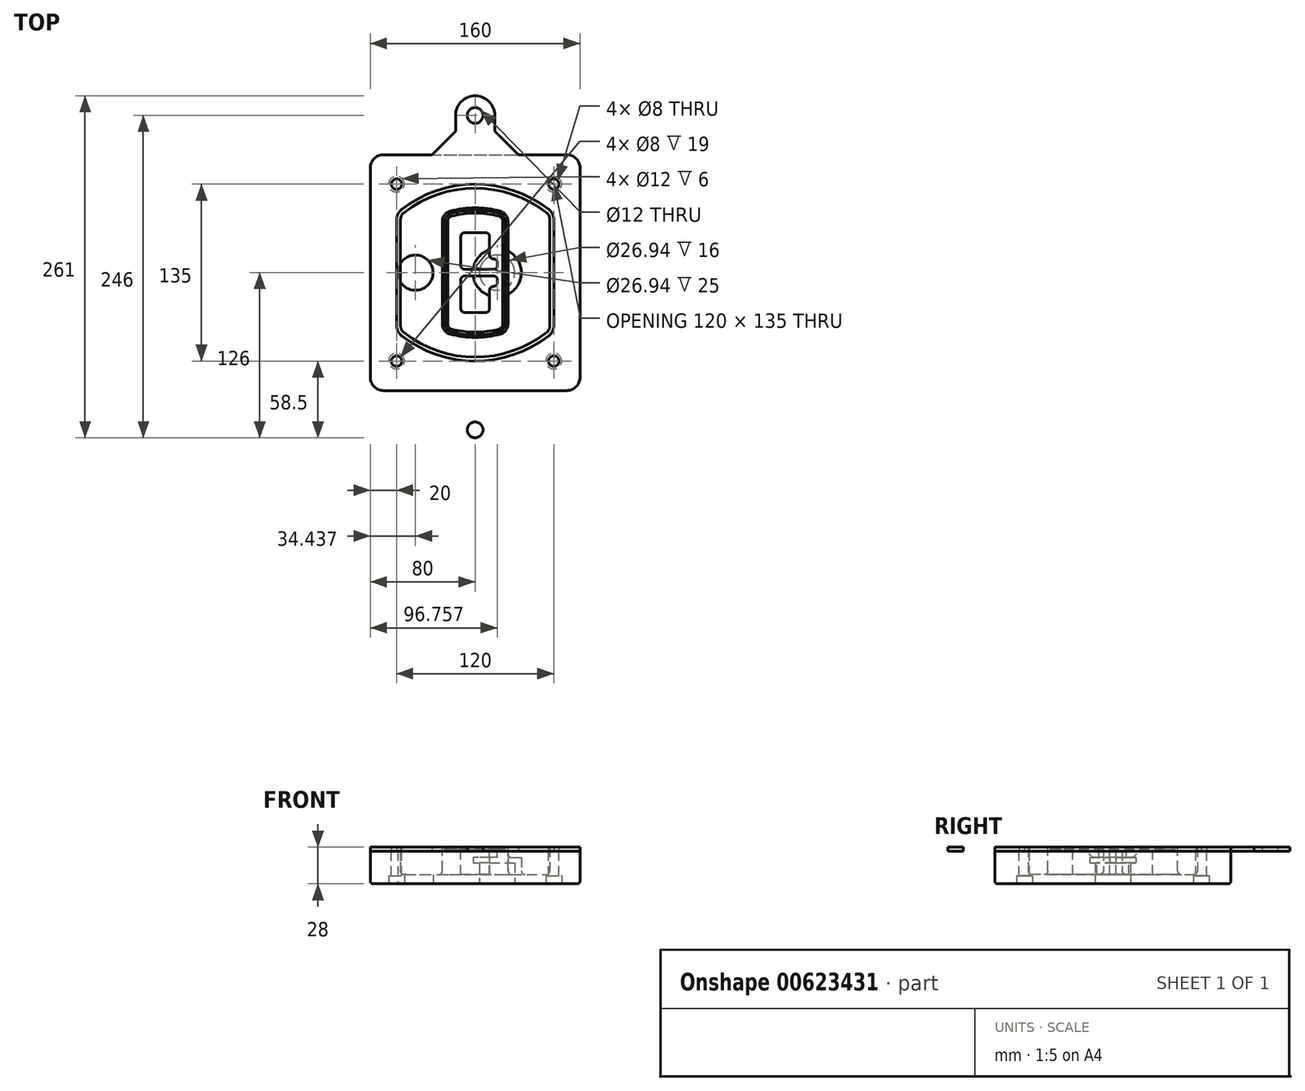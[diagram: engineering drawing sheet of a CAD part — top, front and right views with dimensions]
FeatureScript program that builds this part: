
annotation { "Feature Type Name" : "Feature", "Feature Type Description" : "" }
export const myFeature = defineFeature(function(context is Context, id is Id, definition is map)
    precondition{}
    {
        {
            var Q0;
            Q0=qCreatedBy(makeId("Top.planeOp"),FACE);
            var sketch = newSketch(context, id + "F0", { "sketchPlane" : qUnion([Q0])});
            skPoint(sketch, "E0.rect.middle", {"position": v(0, 0) * mm});
            skLineSegment(sketch, "E1.bottom", {"start": v(-70, -90) * mm, "end": v(70, -90) * mm});
            skLineSegment(sketch, "E1.top", {"start": v(-70, 90) * mm, "end": v(70, 90) * mm});
            skLineSegment(sketch, "E1.left", {"start": v(-80, -80) * mm, "end": v(-80, 80) * mm});
            skLineSegment(sketch, "E1.right", {"start": v(80, -80) * mm, "end": v(80, 80) * mm});
            skLineSegment(sketch, "E2", {"start": v(-80, 90) * mm, "end": v(80, -90) * mm, "construction": true});
            skLineSegment(sketch, "E3", {"start": v(80, 90) * mm, "end": v(-80, -90) * mm, "construction": true});
            skCircle(sketch, "E4", {"center": v(-60, 67.5) * mm, "radius": 4 * mm});
            skCircle(sketch, "E5", {"center": v(60, 67.5) * mm, "radius": 4 * mm});
            skCircle(sketch, "E6", {"center": v(60, -67.5) * mm, "radius": 4 * mm});
            skCircle(sketch, "E7", {"center": v(-60, -67.5) * mm, "radius": 4 * mm});
            skLineSegment(sketch, "E8", {"start": v(-60, 67.5) * mm, "end": v(60, 67.5) * mm, "construction": true});
            skLineSegment(sketch, "E9", {"start": v(60, 67.5) * mm, "end": v(60, -67.5) * mm, "construction": true});
            skLineSegment(sketch, "E10", {"start": v(60, -67.5) * mm, "end": v(-60, -67.5) * mm, "construction": true});
            skLineSegment(sketch, "E11", {"start": v(-60, -67.5) * mm, "end": v(-60, 67.5) * mm, "construction": true});
            skLineSegment(sketch, "E12", {"start": v(-60, 40.3) * mm, "end": v(-60, -40.3) * mm});
            skLineSegment(sketch, "E13", {"start": v(60, 40.3) * mm, "end": v(60, -40.3) * mm});
            skArc(sketch, "E14", {"start": v(56.15, 48.18) * mm, "mid": v(0, 67.5) * mm, "end": v(-56.15, 48.18) * mm});
            skArc(sketch, "E15", {"start": v(-56.15, -48.18) * mm, "mid": v(0, -67.5) * mm, "end": v(56.15, -48.18) * mm});
            skLineSegment(sketch, "E16", {"start": v(-60, 0) * mm, "end": v(60, 0) * mm, "construction": true});
            skPoint(sketch, "E17.visualSharp", {"position": v(-60, -45) * mm});
            skArc(sketch, "E17.filletArc", {"start": v(-60, -40.3) * mm, "mid": v(-58.99, -44.68) * mm, "end": v(-56.15, -48.18) * mm});
            skPoint(sketch, "E18.visualSharp", {"position": v(-60, 45) * mm});
            skArc(sketch, "E18.filletArc", {"start": v(-56.15, 48.18) * mm, "mid": v(-58.99, 44.68) * mm, "end": v(-60, 40.3) * mm});
            skPoint(sketch, "E19.visualSharp", {"position": v(60, 45) * mm});
            skArc(sketch, "E19.filletArc", {"start": v(60, 40.3) * mm, "mid": v(58.99, 44.68) * mm, "end": v(56.15, 48.18) * mm});
            skPoint(sketch, "E20.visualSharp", {"position": v(60, -45) * mm});
            skArc(sketch, "E20.filletArc", {"start": v(56.15, -48.18) * mm, "mid": v(58.99, -44.68) * mm, "end": v(60, -40.3) * mm});
            skPoint(sketch, "E21.visualSharp", {"position": v(-80, 90) * mm});
            skArc(sketch, "E21.filletArc", {"start": v(-70, 90) * mm, "mid": v(-77.07, 87.07) * mm, "end": v(-80, 80) * mm});
            skPoint(sketch, "E22.visualSharp", {"position": v(80, 90) * mm});
            skArc(sketch, "E22.filletArc", {"start": v(80, 80) * mm, "mid": v(77.07, 87.07) * mm, "end": v(70, 90) * mm});
            skPoint(sketch, "E23.visualSharp", {"position": v(80, -90) * mm});
            skArc(sketch, "E23.filletArc", {"start": v(70, -90) * mm, "mid": v(77.07, -87.07) * mm, "end": v(80, -80) * mm});
            skPoint(sketch, "E24.visualSharp", {"position": v(-80, -90) * mm});
            skArc(sketch, "E24.filletArc", {"start": v(-80, -80) * mm, "mid": v(-77.07, -87.07) * mm, "end": v(-70, -90) * mm});
            skArc(sketch, "E25.0", {"start": v(57, 40.3) * mm, "mid": v(56.3, 43.36) * mm, "end": v(54.3, 45.81) * mm});
            skLineSegment(sketch, "E25.1", {"start": v(57, 40.3) * mm, "end": v(57, -40.3) * mm});
            skArc(sketch, "E25.2", {"start": v(54.3, -45.81) * mm, "mid": v(56.3, -43.36) * mm, "end": v(57, -40.3) * mm});
            skArc(sketch, "E25.3", {"start": v(-54.3, -45.81) * mm, "mid": v(0, -64.5) * mm, "end": v(54.3, -45.81) * mm});
            skArc(sketch, "E25.4", {"start": v(-57, -40.3) * mm, "mid": v(-56.3, -43.36) * mm, "end": v(-54.3, -45.81) * mm});
            skArc(sketch, "E25.5", {"start": v(54.3, 45.81) * mm, "mid": v(0, 64.5) * mm, "end": v(-54.3, 45.81) * mm});
            skLineSegment(sketch, "E25.6", {"start": v(-57, 40.3) * mm, "end": v(-57, -40.3) * mm});
            skArc(sketch, "E25.7", {"start": v(-54.3, 45.81) * mm, "mid": v(-56.3, 43.36) * mm, "end": v(-57, 40.3) * mm});
            skArc(sketch, "E26.0", {"start": v(-58.62, 51.33) * mm, "mid": v(-62.58, 46.43) * mm, "end": v(-64, 40.3) * mm});
            skArc(sketch, "E26.1", {"start": v(58.62, 51.33) * mm, "mid": v(0, 71.5) * mm, "end": v(-58.62, 51.33) * mm});
            skArc(sketch, "E26.2", {"start": v(64, 40.3) * mm, "mid": v(62.58, 46.43) * mm, "end": v(58.62, 51.33) * mm});
            skLineSegment(sketch, "E26.3", {"start": v(64, 40.3) * mm, "end": v(64, -40.3) * mm});
            skArc(sketch, "E26.4", {"start": v(58.62, -51.33) * mm, "mid": v(62.58, -46.43) * mm, "end": v(64, -40.3) * mm});
            skLineSegment(sketch, "E26.5", {"start": v(-64, 40.3) * mm, "end": v(-64, -40.3) * mm});
            skArc(sketch, "E26.6", {"start": v(-58.62, -51.33) * mm, "mid": v(0, -71.5) * mm, "end": v(58.62, -51.33) * mm});
            skArc(sketch, "E26.7", {"start": v(-64, -40.3) * mm, "mid": v(-62.58, -46.43) * mm, "end": v(-58.62, -51.33) * mm});
            skSolve(sketch);
        }
        {
            var Q0;
            Q0=makeQuery(id+"F0.imprint","IMPRINT",FACE,{"disambiguationData":[TD([[makeQuery(id+"F0.imprint","IMPRINT",EDGE,{"derivedFrom":sQuery(id+"F0.wireOp",EDGE,"E1.bottom")}),1.0]])]});
            var Q1;
            Q1=makeQuery(id+"F0.imprint","IMPRINT",FACE,{"disambiguationData":[TD([[makeQuery(id+"F0.imprint","IMPRINT",EDGE,{"derivedFrom":sQuery(id+"F0.wireOp",EDGE,"E12")}),1.0]])]});
            var Q2;
            Q2=makeQuery(id+"F0.imprint","IMPRINT",FACE,{"disambiguationData":[TD([[makeQuery(id+"F0.imprint","IMPRINT",EDGE,{"derivedFrom":sQuery(id+"F0.wireOp",EDGE,"E25.0")}),1.0]])]});
            var Q3;
            Q3=makeQuery(id+"F0.imprint","IMPRINT",FACE,{"disambiguationData":[TD([[makeQuery(id+"F0.imprint","IMPRINT",EDGE,{"derivedFrom":sQuery(id+"F0.wireOp",EDGE,"E12")}),-1.0]])]});
            extrude(context, id + "F1", {"entities" : qUnion([Q0, Q1, Q2, Q3]), "oppositeDirection" : true, "depth" : 25 * mm});
        }
        {
            var Q0;
            Q0=makeQuery(id+"F0.imprint","IMPRINT",FACE,{"disambiguationData":[TD([[makeQuery(id+"F0.imprint","IMPRINT",EDGE,{"derivedFrom":sQuery(id+"F0.wireOp",EDGE,"E12")}),1.0]])]});
            extrude(context, id + "F2", {"entities" : qUnion([Q0]), "operationType" : NewBodyOperationType.ADD, "depth" : 3 * mm});
        }
        {
            var Q0;
            Q0=makeQuery(id+"F0.imprint","IMPRINT",FACE,{"disambiguationData":[TD([[makeQuery(id+"F0.imprint","IMPRINT",EDGE,{"derivedFrom":sQuery(id+"F0.wireOp",EDGE,"E25.0")}),1.0]])]});
            extrude(context, id + "F3", {"entities" : qUnion([Q0]), "operationType" : NewBodyOperationType.REMOVE, "oppositeDirection" : true, "depth" : 18 * mm});
        }
        {
            var Q0;
            Q0=makeQuery(id+"F2.opExtrude","CAP_FACE",FACE,{"disambiguationData":[OSD([sQuery(id+"F0.wireOp",EDGE,"E12"),sQuery(id+"F0.wireOp",EDGE,"E13"),sQuery(id+"F0.wireOp",EDGE,"E14"),sQuery(id+"F0.wireOp",EDGE,"E15"),sQuery(id+"F0.wireOp",EDGE,"E17.filletArc"),sQuery(id+"F0.wireOp",EDGE,"E18.filletArc"),sQuery(id+"F0.wireOp",EDGE,"E19.filletArc"),sQuery(id+"F0.wireOp",EDGE,"E20.filletArc"),sQuery(id+"F0.wireOp",EDGE,"E25.0"),sQuery(id+"F0.wireOp",EDGE,"E25.1"),sQuery(id+"F0.wireOp",EDGE,"E25.2"),sQuery(id+"F0.wireOp",EDGE,"E25.3"),sQuery(id+"F0.wireOp",EDGE,"E25.4"),sQuery(id+"F0.wireOp",EDGE,"E25.5"),sQuery(id+"F0.wireOp",EDGE,"E25.6"),sQuery(id+"F0.wireOp",EDGE,"E25.7")])],"isStart":false});
            var sketch = newSketch(context, id + "F4", { "sketchPlane" : qUnion([Q0])});
            skArc(sketch, "E27.0", {"start": v(-19.08, -46.97) * mm, "mid": v(0, -49.5) * mm, "end": v(19.08, -46.97) * mm});
            skArc(sketch, "E28.0", {"start": v(19.08, 46.97) * mm, "mid": v(0, 49.5) * mm, "end": v(-19.08, 46.97) * mm});
            skLineSegment(sketch, "E29", {"start": v(-25, 39.25) * mm, "end": v(-25, -39.25) * mm});
            skLineSegment(sketch, "E30", {"start": v(25, 39.25) * mm, "end": v(25, -39.25) * mm});
            skLineSegment(sketch, "E31", {"start": v(-25, 45.1) * mm, "end": v(25, 45.1) * mm, "construction": true});
            skLineSegment(sketch, "E32", {"start": v(-25, -45.1) * mm, "end": v(25, -45.1) * mm, "construction": true});
            skPoint(sketch, "E33.visualSharp", {"position": v(-25, 45.1) * mm});
            skArc(sketch, "E33.filletArc", {"start": v(-19.08, 46.97) * mm, "mid": v(-23.35, 44.11) * mm, "end": v(-25, 39.25) * mm});
            skPoint(sketch, "E34.visualSharp", {"position": v(25, 45.1) * mm});
            skArc(sketch, "E34.filletArc", {"start": v(25, 39.25) * mm, "mid": v(23.35, 44.11) * mm, "end": v(19.08, 46.97) * mm});
            skPoint(sketch, "E35.visualSharp", {"position": v(25, -45.1) * mm});
            skArc(sketch, "E35.filletArc", {"start": v(19.08, -46.97) * mm, "mid": v(23.35, -44.11) * mm, "end": v(25, -39.25) * mm});
            skPoint(sketch, "E36.visualSharp", {"position": v(-25, -45.1) * mm});
            skArc(sketch, "E36.filletArc", {"start": v(-25, -39.25) * mm, "mid": v(-23.35, -44.11) * mm, "end": v(-19.08, -46.97) * mm});
            skArc(sketch, "E37.0", {"start": v(54.3, 45.81) * mm, "mid": v(0, 64.5) * mm, "end": v(-54.3, 45.81) * mm});
            skArc(sketch, "E37.1", {"start": v(-54.3, 45.81) * mm, "mid": v(-56.3, 43.36) * mm, "end": v(-57, 40.3) * mm});
            skLineSegment(sketch, "E37.2", {"start": v(-57, 40.3) * mm, "end": v(-57, -40.3) * mm});
            skArc(sketch, "E37.3", {"start": v(-57, -40.3) * mm, "mid": v(-56.3, -43.36) * mm, "end": v(-54.3, -45.81) * mm});
            skArc(sketch, "E37.4", {"start": v(-54.3, -45.81) * mm, "mid": v(0, -64.5) * mm, "end": v(54.3, -45.81) * mm});
            skArc(sketch, "E37.5", {"start": v(54.3, -45.81) * mm, "mid": v(56.3, -43.36) * mm, "end": v(57, -40.3) * mm});
            skLineSegment(sketch, "E37.6", {"start": v(57, 40.3) * mm, "end": v(57, -40.3) * mm});
            skArc(sketch, "E37.7", {"start": v(57, 40.3) * mm, "mid": v(56.3, 43.36) * mm, "end": v(54.3, 45.81) * mm});
            skLineSegment(sketch, "E38.0", {"start": v(23, 39.25) * mm, "end": v(23, -39.25) * mm});
            skArc(sketch, "E38.1", {"start": v(18.56, -45.04) * mm, "mid": v(21.76, -42.9) * mm, "end": v(23, -39.25) * mm});
            skArc(sketch, "E38.2", {"start": v(-18.56, -45.04) * mm, "mid": v(0, -47.5) * mm, "end": v(18.56, -45.04) * mm});
            skArc(sketch, "E38.3", {"start": v(-23, -39.25) * mm, "mid": v(-21.76, -42.9) * mm, "end": v(-18.56, -45.04) * mm});
            skLineSegment(sketch, "E38.4", {"start": v(-23, 39.25) * mm, "end": v(-23, -39.25) * mm});
            skArc(sketch, "E38.5", {"start": v(23, 39.25) * mm, "mid": v(21.76, 42.9) * mm, "end": v(18.56, 45.04) * mm});
            skArc(sketch, "E38.6", {"start": v(-18.56, 45.04) * mm, "mid": v(-21.76, 42.9) * mm, "end": v(-23, 39.25) * mm});
            skArc(sketch, "E38.7", {"start": v(18.56, 45.04) * mm, "mid": v(0, 47.5) * mm, "end": v(-18.56, 45.04) * mm});
            skArc(sketch, "E39.0", {"start": v(21, 39.25) * mm, "mid": v(20.18, 41.68) * mm, "end": v(18.04, 43.1) * mm});
            skLineSegment(sketch, "E39.1", {"start": v(21, 39.25) * mm, "end": v(21, -39.25) * mm});
            skArc(sketch, "E39.2", {"start": v(18.04, -43.1) * mm, "mid": v(20.18, -41.68) * mm, "end": v(21, -39.25) * mm});
            skArc(sketch, "E39.3", {"start": v(-18.04, -43.1) * mm, "mid": v(0, -45.5) * mm, "end": v(18.04, -43.1) * mm});
            skArc(sketch, "E39.4", {"start": v(-21, -39.25) * mm, "mid": v(-20.18, -41.68) * mm, "end": v(-18.04, -43.1) * mm});
            skArc(sketch, "E39.5", {"start": v(18.04, 43.1) * mm, "mid": v(0, 45.5) * mm, "end": v(-18.04, 43.1) * mm});
            skLineSegment(sketch, "E39.6", {"start": v(-21, 39.25) * mm, "end": v(-21, -39.25) * mm});
            skArc(sketch, "E39.7", {"start": v(-18.04, 43.1) * mm, "mid": v(-20.18, 41.68) * mm, "end": v(-21, 39.25) * mm});
            skLineSegment(sketch, "E40", {"start": v(-25, 0) * mm, "end": v(25, 0) * mm, "construction": true});
            skLineSegment(sketch, "E41", {"start": v(-11, 5.5) * mm, "end": v(-11, 27.5) * mm});
            skLineSegment(sketch, "E42", {"start": v(-8, 30.5) * mm, "end": v(8, 30.5) * mm});
            skLineSegment(sketch, "E43", {"start": v(11, 27.5) * mm, "end": v(11, 13.5) * mm});
            skLineSegment(sketch, "E44", {"start": v(14, 10.5) * mm, "end": v(14, 10.5) * mm});
            skLineSegment(sketch, "E45", {"start": v(17, 7.5) * mm, "end": v(17, 5.5) * mm});
            skLineSegment(sketch, "E46", {"start": v(14, 2.5) * mm, "end": v(-8, 2.5) * mm});
            skPoint(sketch, "E47.visualSharp", {"position": v(-11, 30.5) * mm});
            skArc(sketch, "E47.filletArc", {"start": v(-8, 30.5) * mm, "mid": v(-10.12, 29.62) * mm, "end": v(-11, 27.5) * mm});
            skPoint(sketch, "E48.visualSharp", {"position": v(11, 30.5) * mm});
            skArc(sketch, "E48.filletArc", {"start": v(11, 27.5) * mm, "mid": v(10.12, 29.62) * mm, "end": v(8, 30.5) * mm});
            skPoint(sketch, "E49.visualSharp", {"position": v(11, 10.5) * mm});
            skArc(sketch, "E49.filletArc", {"start": v(11, 13.5) * mm, "mid": v(11.88, 11.38) * mm, "end": v(14, 10.5) * mm});
            skPoint(sketch, "E50.visualSharp", {"position": v(17, 10.5) * mm});
            skArc(sketch, "E50.filletArc", {"start": v(17, 7.5) * mm, "mid": v(16.12, 9.62) * mm, "end": v(14, 10.5) * mm});
            skPoint(sketch, "E51.visualSharp", {"position": v(17, 2.5) * mm});
            skArc(sketch, "E51.filletArc", {"start": v(14, 2.5) * mm, "mid": v(16.12, 3.38) * mm, "end": v(17, 5.5) * mm});
            skPoint(sketch, "E52.visualSharp", {"position": v(-11, 2.5) * mm});
            skArc(sketch, "E52.filletArc", {"start": v(-11, 5.5) * mm, "mid": v(-10.12, 3.38) * mm, "end": v(-8, 2.5) * mm});
            skLineSegment(sketch, "E53.0.MirrorCS", {"start": v(14, -2.5) * mm, "end": v(-8, -2.5) * mm});
            skArc(sketch, "E54.0.MirrorCS", {"start": v(-11, -5.5) * mm, "mid": v(-10.12, -3.38) * mm, "end": v(-8, -2.5) * mm});
            skLineSegment(sketch, "E55.0.MirrorCS", {"start": v(-11, -5.5) * mm, "end": v(-11, -27.5) * mm});
            skArc(sketch, "E56.0.MirrorCS", {"start": v(-8, -30.5) * mm, "mid": v(-10.12, -29.62) * mm, "end": v(-11, -27.5) * mm});
            skLineSegment(sketch, "E57.0.MirrorCS", {"start": v(-8, -30.5) * mm, "end": v(8, -30.5) * mm});
            skArc(sketch, "E58.0.MirrorCS", {"start": v(11, -27.5) * mm, "mid": v(10.12, -29.62) * mm, "end": v(8, -30.5) * mm});
            skLineSegment(sketch, "E59.0.MirrorCS", {"start": v(11, -27.5) * mm, "end": v(11, -13.5) * mm});
            skArc(sketch, "E60.0.MirrorCS", {"start": v(11, -13.5) * mm, "mid": v(11.88, -11.38) * mm, "end": v(14, -10.5) * mm});
            skArc(sketch, "E61.0.MirrorCS", {"start": v(17, -7.5) * mm, "mid": v(16.12, -9.62) * mm, "end": v(14, -10.5) * mm});
            skLineSegment(sketch, "E62.0.MirrorCS", {"start": v(17, -7.5) * mm, "end": v(17, -5.5) * mm});
            skArc(sketch, "E63.0.MirrorCS", {"start": v(14, -2.5) * mm, "mid": v(16.12, -3.38) * mm, "end": v(17, -5.5) * mm});
            skSolve(sketch);
        }
        {
            var Q0;
            Q0=makeQuery(id+"F4.imprint","IMPRINT",FACE,{"disambiguationData":[TD([[makeQuery(id+"F4.imprint","IMPRINT",EDGE,{"derivedFrom":sQuery(id+"F4.wireOp",EDGE,"E27.0")}),1.0]])]});
            var Q1;
            Q1=makeQuery(id+"F4.imprint","IMPRINT",FACE,{"disambiguationData":[TD([[makeQuery(id+"F4.imprint","IMPRINT",EDGE,{"derivedFrom":sQuery(id+"F4.wireOp",EDGE,"E38.0")}),-1.0]])]});
            var Q2;
            Q2=makeQuery(id+"F4.imprint","IMPRINT",FACE,{"disambiguationData":[TD([[makeQuery(id+"F4.imprint","IMPRINT",EDGE,{"derivedFrom":sQuery(id+"F4.wireOp",EDGE,"E39.0")}),1.0]])]});
            extrude(context, id + "F5", {"entities" : qUnion([Q0, Q1, Q2]), "operationType" : NewBodyOperationType.ADD, "endBound" : BoundingType.UP_TO_NEXT, "oppositeDirection" : true, "depth" : 25 * mm});
        }
        {
            var Q0;
            Q0=makeQuery(id+"F4.imprint","IMPRINT",FACE,{"disambiguationData":[TD([[makeQuery(id+"F4.imprint","IMPRINT",EDGE,{"derivedFrom":sQuery(id+"F4.wireOp",EDGE,"E38.0")}),-1.0]])]});
            extrude(context, id + "F6", {"entities" : qUnion([Q0]), "operationType" : NewBodyOperationType.REMOVE, "oppositeDirection" : true, "depth" : 2 * mm});
        }
        {
            var Q0;
            Q0=makeQuery(id+"F1.opExtrude","CAP_FACE",FACE,{"disambiguationData":[OSD([sQuery(id+"F0.wireOp",EDGE,"E1.bottom"),sQuery(id+"F0.wireOp",EDGE,"E1.top"),sQuery(id+"F0.wireOp",EDGE,"E1.left"),sQuery(id+"F0.wireOp",EDGE,"E1.right"),sQuery(id+"F0.wireOp",EDGE,"E4"),sQuery(id+"F0.wireOp",EDGE,"E5"),sQuery(id+"F0.wireOp",EDGE,"E6"),sQuery(id+"F0.wireOp",EDGE,"E7"),sQuery(id+"F0.wireOp",EDGE,"E21.filletArc"),sQuery(id+"F0.wireOp",EDGE,"E22.filletArc"),sQuery(id+"F0.wireOp",EDGE,"E23.filletArc"),sQuery(id+"F0.wireOp",EDGE,"E24.filletArc")])],"isStart":false});
            var sketch = newSketch(context, id + "F7", { "sketchPlane" : qUnion([Q0])});
            skCircle(sketch, "E64", {"center": v(16.76, 0) * mm, "radius": 13.47 * mm});
            skCircle(sketch, "E65", {"center": v(-45.56, 0) * mm, "radius": 13.47 * mm});
            skLineSegment(sketch, "E66", {"start": v(80, 0) * mm, "end": v(-80, 0) * mm});
            skCircle(sketch, "E67", {"center": v(16.76, 0) * mm, "radius": 18.47 * mm});
            skCircle(sketch, "E68", {"center": v(60, -67.5) * mm, "radius": 6 * mm});
            skCircle(sketch, "E69", {"center": v(-60, -67.5) * mm, "radius": 6 * mm});
            skCircle(sketch, "E70", {"center": v(-60, 67.5) * mm, "radius": 6 * mm});
            skCircle(sketch, "E71", {"center": v(60, 67.5) * mm, "radius": 6 * mm});
            skSolve(sketch);
        }
        {
            var Q0;
            {var subQ1=sQuery(id+"F7.wireOp",EDGE,"E66");var subQ4=sQuery(id+"F7.wireOp",EDGE,"E64");var subQ6=makeQuery(id+"F7.imprint","INTERSECT",VERTEX,{"disambiguationData":[OD(0.0)],"derivedFrom":[subQ4,subQ1]});Q0=makeQuery(id+"F7.imprint","IMPRINT",FACE,{"disambiguationData":[TD([[makeQuery(id+"F7.imprint","IMPRINT",EDGE,{"disambiguationData":[TD([[subQ6,-1.0]])],"derivedFrom":subQ4}),-1.0]])]});}
            var Q1;
            {var subQ0=sQuery(id+"F7.wireOp",EDGE,"E66");var subQ1=sQuery(id+"F7.wireOp",EDGE,"E64");var subQ3=makeQuery(id+"F7.imprint","INTERSECT",VERTEX,{"disambiguationData":[OD(0.0)],"derivedFrom":[subQ1,subQ0]});Q1=makeQuery(id+"F7.imprint","IMPRINT",FACE,{"disambiguationData":[TD([[makeQuery(id+"F7.imprint","IMPRINT",EDGE,{"disambiguationData":[TD([[subQ3,-1.0]])],"derivedFrom":subQ1}),1.0]])]});}
            var Q2;
            {var subQ0=sQuery(id+"F7.wireOp",EDGE,"E66");var subQ1=sQuery(id+"F7.wireOp",EDGE,"E64");var subQ3=makeQuery(id+"F7.imprint","INTERSECT",VERTEX,{"disambiguationData":[OD(0.0)],"derivedFrom":[subQ1,subQ0]});Q2=makeQuery(id+"F7.imprint","IMPRINT",FACE,{"disambiguationData":[TD([[makeQuery(id+"F7.imprint","IMPRINT",EDGE,{"disambiguationData":[TD([[subQ3,1.0]])],"derivedFrom":subQ1}),1.0]])]});}
            var Q3;
            {var subQ1=sQuery(id+"F7.wireOp",EDGE,"E66");var subQ4=sQuery(id+"F7.wireOp",EDGE,"E64");var subQ6=makeQuery(id+"F7.imprint","INTERSECT",VERTEX,{"disambiguationData":[OD(0.0)],"derivedFrom":[subQ4,subQ1]});Q3=makeQuery(id+"F7.imprint","IMPRINT",FACE,{"disambiguationData":[TD([[makeQuery(id+"F7.imprint","IMPRINT",EDGE,{"disambiguationData":[TD([[subQ6,1.0]])],"derivedFrom":subQ4}),-1.0]])]});}
            extrude(context, id + "F8", {"entities" : qUnion([Q0, Q1, Q2, Q3]), "operationType" : NewBodyOperationType.ADD, "oppositeDirection" : true, "depth" : 20 * mm});
        }
        {
            var Q0;
            {var subQ0=sQuery(id+"F7.wireOp",EDGE,"E66");var subQ1=sQuery(id+"F7.wireOp",EDGE,"E64");var subQ3=makeQuery(id+"F7.imprint","INTERSECT",VERTEX,{"disambiguationData":[OD(0.0)],"derivedFrom":[subQ1,subQ0]});Q0=makeQuery(id+"F7.imprint","IMPRINT",FACE,{"disambiguationData":[TD([[makeQuery(id+"F7.imprint","IMPRINT",EDGE,{"disambiguationData":[TD([[subQ3,-1.0]])],"derivedFrom":subQ1}),1.0]])]});}
            var Q1;
            {var subQ0=sQuery(id+"F7.wireOp",EDGE,"E66");var subQ1=sQuery(id+"F7.wireOp",EDGE,"E64");var subQ3=makeQuery(id+"F7.imprint","INTERSECT",VERTEX,{"disambiguationData":[OD(0.0)],"derivedFrom":[subQ1,subQ0]});Q1=makeQuery(id+"F7.imprint","IMPRINT",FACE,{"disambiguationData":[TD([[makeQuery(id+"F7.imprint","IMPRINT",EDGE,{"disambiguationData":[TD([[subQ3,1.0]])],"derivedFrom":subQ1}),1.0]])]});}
            extrude(context, id + "F9", {"entities" : qUnion([Q0, Q1]), "operationType" : NewBodyOperationType.REMOVE, "oppositeDirection" : true, "depth" : 16 * mm});
        }
        {
            var Q0;
            {var subQ0=sQuery(id+"F7.wireOp",EDGE,"E66");var subQ1=sQuery(id+"F7.wireOp",EDGE,"E65");var subQ3=makeQuery(id+"F7.imprint","INTERSECT",VERTEX,{"disambiguationData":[OD(0.0)],"derivedFrom":[subQ1,subQ0]});Q0=makeQuery(id+"F7.imprint","IMPRINT",FACE,{"disambiguationData":[TD([[makeQuery(id+"F7.imprint","IMPRINT",EDGE,{"disambiguationData":[TD([[subQ3,-1.0]])],"derivedFrom":subQ1}),1.0]])]});}
            var Q1;
            {var subQ0=sQuery(id+"F7.wireOp",EDGE,"E66");var subQ1=sQuery(id+"F7.wireOp",EDGE,"E65");var subQ3=makeQuery(id+"F7.imprint","INTERSECT",VERTEX,{"disambiguationData":[OD(0.0)],"derivedFrom":[subQ1,subQ0]});Q1=makeQuery(id+"F7.imprint","IMPRINT",FACE,{"disambiguationData":[TD([[makeQuery(id+"F7.imprint","IMPRINT",EDGE,{"disambiguationData":[TD([[subQ3,1.0]])],"derivedFrom":subQ1}),1.0]])]});}
            extrude(context, id + "F10", {"entities" : qUnion([Q0, Q1]), "operationType" : NewBodyOperationType.REMOVE, "oppositeDirection" : true, "depth" : 25 * mm});
        }
        {
            var Q0;
            Q0=makeQuery(id+"F7.imprint","IMPRINT",FACE,{"disambiguationData":[TD([[makeQuery(id+"F7.imprint","IMPRINT",EDGE,{"derivedFrom":sQuery(id+"F7.wireOp",EDGE,"E68")}),1.0]])]});
            var Q1;
            Q1=makeQuery(id+"F7.imprint","IMPRINT",FACE,{"disambiguationData":[TD([[makeQuery(id+"F7.imprint","IMPRINT",EDGE,{"derivedFrom":makeQuery(id+"F1.opExtrude","CAP_EDGE",EDGE,{"disambiguationData":[OSD([sQuery(id+"F0.wireOp",EDGE,"E5")])],"isStart":false})}),-1.0]])]});
            var Q2;
            Q2=makeQuery(id+"F7.imprint","IMPRINT",FACE,{"disambiguationData":[TD([[makeQuery(id+"F7.imprint","IMPRINT",EDGE,{"derivedFrom":sQuery(id+"F7.wireOp",EDGE,"E69")}),1.0]])]});
            var Q3;
            Q3=makeQuery(id+"F7.imprint","IMPRINT",FACE,{"disambiguationData":[TD([[makeQuery(id+"F7.imprint","IMPRINT",EDGE,{"derivedFrom":makeQuery(id+"F1.opExtrude","CAP_EDGE",EDGE,{"disambiguationData":[OSD([sQuery(id+"F0.wireOp",EDGE,"E4")])],"isStart":false})}),-1.0]])]});
            var Q4;
            Q4=makeQuery(id+"F7.imprint","IMPRINT",FACE,{"disambiguationData":[TD([[makeQuery(id+"F7.imprint","IMPRINT",EDGE,{"derivedFrom":sQuery(id+"F7.wireOp",EDGE,"E70")}),1.0]])]});
            var Q5;
            Q5=makeQuery(id+"F7.imprint","IMPRINT",FACE,{"disambiguationData":[TD([[makeQuery(id+"F7.imprint","IMPRINT",EDGE,{"derivedFrom":makeQuery(id+"F1.opExtrude","CAP_EDGE",EDGE,{"disambiguationData":[OSD([sQuery(id+"F0.wireOp",EDGE,"E7")])],"isStart":false})}),-1.0]])]});
            var Q6;
            Q6=makeQuery(id+"F7.imprint","IMPRINT",FACE,{"disambiguationData":[TD([[makeQuery(id+"F7.imprint","IMPRINT",EDGE,{"derivedFrom":sQuery(id+"F7.wireOp",EDGE,"E71")}),1.0]])]});
            var Q7;
            Q7=makeQuery(id+"F7.imprint","IMPRINT",FACE,{"disambiguationData":[TD([[makeQuery(id+"F7.imprint","IMPRINT",EDGE,{"derivedFrom":makeQuery(id+"F1.opExtrude","CAP_EDGE",EDGE,{"disambiguationData":[OSD([sQuery(id+"F0.wireOp",EDGE,"E6")])],"isStart":false})}),-1.0]])]});
            extrude(context, id + "F11", {"entities" : qUnion([Q0, Q1, Q2, Q3, Q4, Q5, Q6, Q7]), "operationType" : NewBodyOperationType.REMOVE, "oppositeDirection" : true, "depth" : 6 * mm});
        }
        {
            var Q0;
            Q0=makeQuery(id+"F9.boolean.opBoolean","COPY",FACE,{"derivedFrom":makeQuery(id+"F9.opExtrude","CAP_FACE",FACE,{"disambiguationData":[OSD([sQuery(id+"F7.wireOp",EDGE,"E64")])],"isStart":false})});
            var sketch = newSketch(context, id + "F12", { "sketchPlane" : qUnion([Q0])});
            skArc(sketch, "E72.0", {"start": v(11, 17.55) * mm, "mid": v(2.57, 11.82) * mm, "end": v(-1.54, 2.5) * mm});
            skArc(sketch, "E72.1", {"start": v(-1.54, -2.5) * mm, "mid": v(2.57, -11.82) * mm, "end": v(11, -17.55) * mm});
            skLineSegment(sketch, "E73", {"start": v(-1.54, -2.5) * mm, "end": v(14, -2.5) * mm});
            skLineSegment(sketch, "E74.0", {"start": v(14, 2.5) * mm, "end": v(-1.54, 2.5) * mm});
            skArc(sketch, "E74.1", {"start": v(14, 2.5) * mm, "mid": v(16.12, 3.38) * mm, "end": v(17, 5.5) * mm});
            skLineSegment(sketch, "E74.2", {"start": v(17, 7.5) * mm, "end": v(17, 5.5) * mm});
            skArc(sketch, "E74.3", {"start": v(17, 7.5) * mm, "mid": v(16.12, 9.62) * mm, "end": v(14, 10.5) * mm});
            skArc(sketch, "E74.4", {"start": v(11, 13.5) * mm, "mid": v(11.88, 11.38) * mm, "end": v(14, 10.5) * mm});
            skLineSegment(sketch, "E74.5", {"start": v(11, 17.55) * mm, "end": v(11, 13.5) * mm});
            skLineSegment(sketch, "E74.7", {"start": v(14, -2.5) * mm, "end": v(-1.54, -2.5) * mm});
            skArc(sketch, "E74.8", {"start": v(14, -2.5) * mm, "mid": v(16.12, -3.38) * mm, "end": v(17, -5.5) * mm});
            skLineSegment(sketch, "E74.9", {"start": v(17, -7.5) * mm, "end": v(17, -5.5) * mm});
            skArc(sketch, "E74.10", {"start": v(17, -7.5) * mm, "mid": v(16.12, -9.62) * mm, "end": v(14, -10.5) * mm});
            skArc(sketch, "E74.11", {"start": v(11, -13.5) * mm, "mid": v(11.88, -11.38) * mm, "end": v(14, -10.5) * mm});
            skLineSegment(sketch, "E74.12", {"start": v(11, -17.55) * mm, "end": v(11, -13.5) * mm});
            skPoint(sketch, "E75.orphan", {"position": v(11, -27.5) * mm});
            skPoint(sketch, "E76.orphan", {"position": v(-8, -2.5) * mm});
            skPoint(sketch, "E77.orphan", {"position": v(-8, 2.5) * mm});
            skPoint(sketch, "E78.orphan", {"position": v(11, 27.5) * mm});
            skSolve(sketch);
        }
        {
            var Q0;
            {var subQ7=sQuery(id+"F12.wireOp",EDGE,"E72.0");var subQ14=sQuery(id+"F12.wireOp",EDGE,"E72.1");var subQ16=sQuery(id+"F12.wireOp",EDGE,"E74.1");var subQ18=sQuery(id+"F12.wireOp",EDGE,"E74.8");Q0=qUnion([makeQuery(id+"F12.imprint","IMPRINT",FACE,{"disambiguationData":[TD([[makeQuery(id+"F12.imprint","IMPRINT",EDGE,{"derivedFrom":subQ7}),1.0]])]}),makeQuery(id+"F12.imprint","IMPRINT",FACE,{"disambiguationData":[TD([[makeQuery(id+"F12.imprint","IMPRINT",EDGE,{"derivedFrom":subQ14}),1.0]])]}),makeQuery(id+"F12.imprint","IMPRINT",FACE,{"disambiguationData":[TD([[makeQuery(id+"F12.imprint","IMPRINT",EDGE,{"derivedFrom":subQ16}),1.0]])]}),makeQuery(id+"F12.imprint","IMPRINT",FACE,{"disambiguationData":[TD([[makeQuery(id+"F12.imprint","IMPRINT",EDGE,{"derivedFrom":subQ18}),-1.0]])]})]);}
            var Q1;
            Q1=makeQuery(id+"F5.boolean.opBoolean","SPLIT",FACE,{"disambiguationData":[TD([makeQuery(id+"F5.opExtrude","SWEPT_FACE",FACE,{"disambiguationData":[OSD([sQuery(id+"F4.wireOp",EDGE,"E41")])]})])],"derivedFrom":makeQuery(id+"F3.boolean.opBoolean","COPY",FACE,{"derivedFrom":makeQuery(id+"F3.opExtrude","CAP_FACE",FACE,{"disambiguationData":[OSD([sQuery(id+"F0.wireOp",EDGE,"E25.0"),sQuery(id+"F0.wireOp",EDGE,"E25.1"),sQuery(id+"F0.wireOp",EDGE,"E25.2"),sQuery(id+"F0.wireOp",EDGE,"E25.3"),sQuery(id+"F0.wireOp",EDGE,"E25.4"),sQuery(id+"F0.wireOp",EDGE,"E25.5"),sQuery(id+"F0.wireOp",EDGE,"E25.6"),sQuery(id+"F0.wireOp",EDGE,"E25.7")])],"isStart":false})})});
            extrude(context, id + "F13", {"entities" : qUnion([Q0]), "operationType" : NewBodyOperationType.REMOVE, "endBound" : BoundingType.UP_TO_SURFACE, "endBoundEntityFace" : qUnion([Q1]), "depth" : 25 * mm});
        }
        {
            var Q0;
            Q0=makeQuery(id+"F3.boolean.opBoolean","COPY",EDGE,{"derivedFrom":makeQuery(id+"F3.opExtrude","CAP_EDGE",EDGE,{"disambiguationData":[OSD([sQuery(id+"F0.wireOp",EDGE,"E25.6")])],"isStart":false})});
            var Q1;
            Q1=makeQuery(id+"F8.boolean.opBoolean","INTERSECT",EDGE,{"derivedFrom":[makeQuery(id+"F5.opExtrude","SWEPT_FACE",FACE,{"disambiguationData":[OSD([sQuery(id+"F4.wireOp",EDGE,"E30")])]}),makeQuery(id+"F8.opExtrude","CAP_FACE",FACE,{"disambiguationData":[OSD([sQuery(id+"F7.wireOp",EDGE,"E67")])],"isStart":false})]});
            var Q2;
            Q2=makeQuery(id+"F8.boolean.opBoolean","INTERSECT",EDGE,{"disambiguationData":[OD(1.0)],"derivedFrom":[makeQuery(id+"F5.opExtrude","SWEPT_FACE",FACE,{"disambiguationData":[OSD([sQuery(id+"F4.wireOp",EDGE,"E30")])]}),makeQuery(id+"F8.opExtrude","SWEPT_FACE",FACE,{"disambiguationData":[OSD([sQuery(id+"F7.wireOp",EDGE,"E67")])]})]});
            var Q3;
            {var subQ0=sQuery(id+"F4.wireOp",EDGE,"E30");Q3=makeQuery(id+"F8.boolean.opBoolean","SPLIT",EDGE,{"disambiguationData":[TD([makeQuery(id+"F5.opExtrude","SWEPT_FACE",FACE,{"disambiguationData":[OSD([sQuery(id+"F4.wireOp",EDGE,"E35.filletArc")])]})])],"derivedFrom":makeQuery(id+"F5.opExtrude","CAP_EDGE",EDGE,{"disambiguationData":[OSD([subQ0])],"isStart":false})});}
            var Q4;
            {var subQ0=sQuery(id+"F0.wireOp",EDGE,"E25.7");var subQ1=sQuery(id+"F0.wireOp",EDGE,"E25.1");var subQ2=sQuery(id+"F0.wireOp",EDGE,"E25.6");var subQ3=sQuery(id+"F0.wireOp",EDGE,"E25.5");var subQ4=sQuery(id+"F0.wireOp",EDGE,"E25.4");var subQ5=sQuery(id+"F0.wireOp",EDGE,"E25.0");var subQ6=sQuery(id+"F0.wireOp",EDGE,"E25.2");var subQ7=sQuery(id+"F0.wireOp",EDGE,"E25.3");Q4=makeQuery(id+"F8.boolean.opBoolean","INTERSECT",EDGE,{"derivedFrom":[makeQuery(id+"F5.boolean.opBoolean","SPLIT",FACE,{"disambiguationData":[TD([makeQuery(id+"F2.opExtrude","SWEPT_FACE",FACE,{"disambiguationData":[OSD([subQ5])]})])],"derivedFrom":makeQuery(id+"F3.boolean.opBoolean","COPY",FACE,{"derivedFrom":makeQuery(id+"F3.opExtrude","CAP_FACE",FACE,{"disambiguationData":[OSD([subQ5,subQ1,subQ6,subQ7,subQ4,subQ3,subQ2,subQ0])],"isStart":false})})}),makeQuery(id+"F8.opExtrude","SWEPT_FACE",FACE,{"disambiguationData":[OSD([sQuery(id+"F7.wireOp",EDGE,"E67")])]})]});}
            var Q5;
            Q5=makeQuery(id+"F8.boolean.opBoolean","INTERSECT",EDGE,{"disambiguationData":[OD(0.0)],"derivedFrom":[makeQuery(id+"F5.opExtrude","SWEPT_FACE",FACE,{"disambiguationData":[OSD([sQuery(id+"F4.wireOp",EDGE,"E30")])]}),makeQuery(id+"F8.opExtrude","SWEPT_FACE",FACE,{"disambiguationData":[OSD([sQuery(id+"F7.wireOp",EDGE,"E67")])]})]});
            fillet(context, id + "F14", {"entities" : qUnion([Q0, Q1, Q2, Q3, Q4, Q5]), "radius" : 3 * mm, "tangentPropagation" : true, "allowEdgeOverflow" : false});
        }
        {
            var Q0;
            Q0=makeQuery(id+"F1.opExtrude","CAP_EDGE",EDGE,{"disambiguationData":[OSD([sQuery(id+"F0.wireOp",EDGE,"E1.bottom")])],"isStart":false});
            fillet(context, id + "F15", {"entities" : qUnion([Q0]), "radius" : 2 * mm, "tangentPropagation" : true, "allowEdgeOverflow" : false});
        }
        {
            var Q0;
            {var subQ0=sQuery(id+"F0.wireOp",EDGE,"E21.filletArc");var subQ1=sQuery(id+"F0.wireOp",EDGE,"E7");var subQ2=sQuery(id+"F0.wireOp",EDGE,"E6");var subQ3=sQuery(id+"F0.wireOp",EDGE,"E5");var subQ4=sQuery(id+"F0.wireOp",EDGE,"E4");var subQ5=sQuery(id+"F0.wireOp",EDGE,"E22.filletArc");var subQ6=sQuery(id+"F0.wireOp",EDGE,"E1.bottom");var subQ7=sQuery(id+"F0.wireOp",EDGE,"E1.right");var subQ8=sQuery(id+"F0.wireOp",EDGE,"E1.top");var subQ9=sQuery(id+"F0.wireOp",EDGE,"E1.left");var subQ10=sQuery(id+"F0.wireOp",EDGE,"E23.filletArc");var subQ11=sQuery(id+"F0.wireOp",EDGE,"E24.filletArc");Q0=makeQuery(id+"F2.boolean.opBoolean","SPLIT",FACE,{"disambiguationData":[TD([makeQuery(id+"F1.opExtrude","SWEPT_FACE",FACE,{"disambiguationData":[OSD([subQ6])]})])],"derivedFrom":makeQuery(id+"F1.opExtrude","CAP_FACE",FACE,{"disambiguationData":[OSD([subQ6,subQ8,subQ9,subQ7,subQ4,subQ3,subQ2,subQ1,subQ0,subQ5,subQ10,subQ11])],"isStart":true})});}
            var sketch = newSketch(context, id + "F16", { "sketchPlane" : qUnion([Q0])});
            skLineSegment(sketch, "E79.0", {"start": v(-70, 90) * mm, "end": v(70, 90) * mm});
            skArc(sketch, "E79.1", {"start": v(-70, 90) * mm, "mid": v(-77.07, 87.07) * mm, "end": v(-80, 80) * mm});
            skLineSegment(sketch, "E79.2", {"start": v(-80, -80) * mm, "end": v(-80, 80) * mm});
            skArc(sketch, "E79.3", {"start": v(-80, -80) * mm, "mid": v(-77.07, -87.07) * mm, "end": v(-70, -90) * mm});
            skLineSegment(sketch, "E79.4", {"start": v(-70, -90) * mm, "end": v(70, -90) * mm});
            skArc(sketch, "E79.5", {"start": v(70, -90) * mm, "mid": v(77.07, -87.07) * mm, "end": v(80, -80) * mm});
            skLineSegment(sketch, "E79.6", {"start": v(80, -80) * mm, "end": v(80, 80) * mm});
            skArc(sketch, "E79.7", {"start": v(80, 80) * mm, "mid": v(77.07, 87.07) * mm, "end": v(70, 90) * mm});
            skCircle(sketch, "E79.8", {"center": v(60, 67.5) * mm, "radius": 4 * mm});
            skCircle(sketch, "E79.9", {"center": v(-60, 67.5) * mm, "radius": 4 * mm});
            skCircle(sketch, "E79.10", {"center": v(-60, -67.5) * mm, "radius": 4 * mm});
            skCircle(sketch, "E79.11", {"center": v(60, -67.5) * mm, "radius": 4 * mm});
            skLineSegment(sketch, "E79.12", {"start": v(-60, 40.3) * mm, "end": v(-60, -40.3) * mm});
            skArc(sketch, "E79.13", {"start": v(-56.15, 48.18) * mm, "mid": v(-58.99, 44.68) * mm, "end": v(-60, 40.3) * mm});
            skArc(sketch, "E79.14", {"start": v(56.15, 48.18) * mm, "mid": v(0, 67.5) * mm, "end": v(-56.15, 48.18) * mm});
            skLineSegment(sketch, "E79.15", {"start": v(60, 40.3) * mm, "end": v(60, -40.3) * mm});
            skArc(sketch, "E79.16", {"start": v(60, 40.3) * mm, "mid": v(58.99, 44.68) * mm, "end": v(56.15, 48.18) * mm});
            skArc(sketch, "E79.17", {"start": v(56.15, -48.18) * mm, "mid": v(58.99, -44.68) * mm, "end": v(60, -40.3) * mm});
            skArc(sketch, "E79.18", {"start": v(-56.15, -48.18) * mm, "mid": v(0, -67.5) * mm, "end": v(56.15, -48.18) * mm});
            skArc(sketch, "E79.19", {"start": v(-60, -40.3) * mm, "mid": v(-58.99, -44.68) * mm, "end": v(-56.15, -48.18) * mm});
            skLineSegment(sketch, "E80", {"start": v(0, 90) * mm, "end": v(0, 120) * mm, "construction": true});
            skCircle(sketch, "E81", {"center": v(0, 120) * mm, "radius": 6 * mm});
            skArc(sketch, "E82", {"start": v(15, 120) * mm, "mid": v(0, 135) * mm, "end": v(-15, 120) * mm});
            skLineSegment(sketch, "E83", {"start": v(-15, 120) * mm, "end": v(-15, 108) * mm});
            skLineSegment(sketch, "E84", {"start": v(-15, 108) * mm, "end": v(-33, 90) * mm});
            skLineSegment(sketch, "E85.MirrorCS", {"start": v(15, 120) * mm, "end": v(15, 108) * mm});
            skLineSegment(sketch, "E86.MirrorCS", {"start": v(15, 108) * mm, "end": v(33, 90) * mm});
            skLineSegment(sketch, "E87", {"start": v(-80, 0) * mm, "end": v(80, 0) * mm, "construction": true});
            skCircle(sketch, "E88.MirrorC", {"center": v(0, -120) * mm, "radius": 6 * mm});
            skLineSegment(sketch, "E89.MirrorCS", {"start": v(15, -120) * mm, "end": v(15, -108) * mm});
            skLineSegment(sketch, "E90.MirrorCS", {"start": v(-15, -120) * mm, "end": v(-15, -108) * mm});
            skLineSegment(sketch, "E91.MirrorCS", {"start": v(-15, -108) * mm, "end": v(-33, -90) * mm});
            skLineSegment(sketch, "E92.MirrorCS", {"start": v(0, -90) * mm, "end": v(0, -120) * mm, "construction": true});
            skArc(sketch, "E93.MirrorCS", {"start": v(15, -120) * mm, "mid": v(0, -135) * mm, "end": v(-15, -120) * mm});
            skLineSegment(sketch, "E94.MirrorCS", {"start": v(15, -108) * mm, "end": v(33, -90) * mm});
            skSolve(sketch);
        }
        {
            var Q0;
            {var subQ0=sQuery(id+"F16.wireOp",EDGE,"E79.1");Q0=makeQuery(id+"F16.imprint","IMPRINT",FACE,{"disambiguationData":[TD([[makeQuery(id+"F16.imprint","IMPRINT",EDGE,{"derivedFrom":subQ0}),1.0]])]});}
            var Q1;
            Q1=makeQuery(id+"F16.imprint","IMPRINT",FACE,{"disambiguationData":[TD([[makeQuery(id+"F16.imprint","IMPRINT",EDGE,{"derivedFrom":sQuery(id+"F16.wireOp",EDGE,"E81")}),-1.0]])]});
            var Q2;
            Q2=makeQuery(id+"F16.imprint","IMPRINT",FACE,{"disambiguationData":[TD([[makeQuery(id+"F16.imprint","IMPRINT",EDGE,{"derivedFrom":sQuery(id+"F16.wireOp",EDGE,"E88.MirrorC")}),1.0]])]});
            var Q3;
            Q3=makeQuery(id+"F2.opExtrude","CAP_FACE",FACE,{"disambiguationData":[OSD([sQuery(id+"F0.wireOp",EDGE,"E12"),sQuery(id+"F0.wireOp",EDGE,"E13"),sQuery(id+"F0.wireOp",EDGE,"E14"),sQuery(id+"F0.wireOp",EDGE,"E15"),sQuery(id+"F0.wireOp",EDGE,"E17.filletArc"),sQuery(id+"F0.wireOp",EDGE,"E18.filletArc"),sQuery(id+"F0.wireOp",EDGE,"E19.filletArc"),sQuery(id+"F0.wireOp",EDGE,"E20.filletArc"),sQuery(id+"F0.wireOp",EDGE,"E25.0"),sQuery(id+"F0.wireOp",EDGE,"E25.1"),sQuery(id+"F0.wireOp",EDGE,"E25.2"),sQuery(id+"F0.wireOp",EDGE,"E25.3"),sQuery(id+"F0.wireOp",EDGE,"E25.4"),sQuery(id+"F0.wireOp",EDGE,"E25.5"),sQuery(id+"F0.wireOp",EDGE,"E25.6"),sQuery(id+"F0.wireOp",EDGE,"E25.7")])],"isStart":false});
            extrude(context, id + "F17", {"entities" : qUnion([Q0, Q1, Q2]), "endBound" : BoundingType.UP_TO_SURFACE, "depth" : 25 * mm, "endBoundEntityFace" : qUnion([Q3]), "offsetDistance" : 25 * mm});
        }
    });
